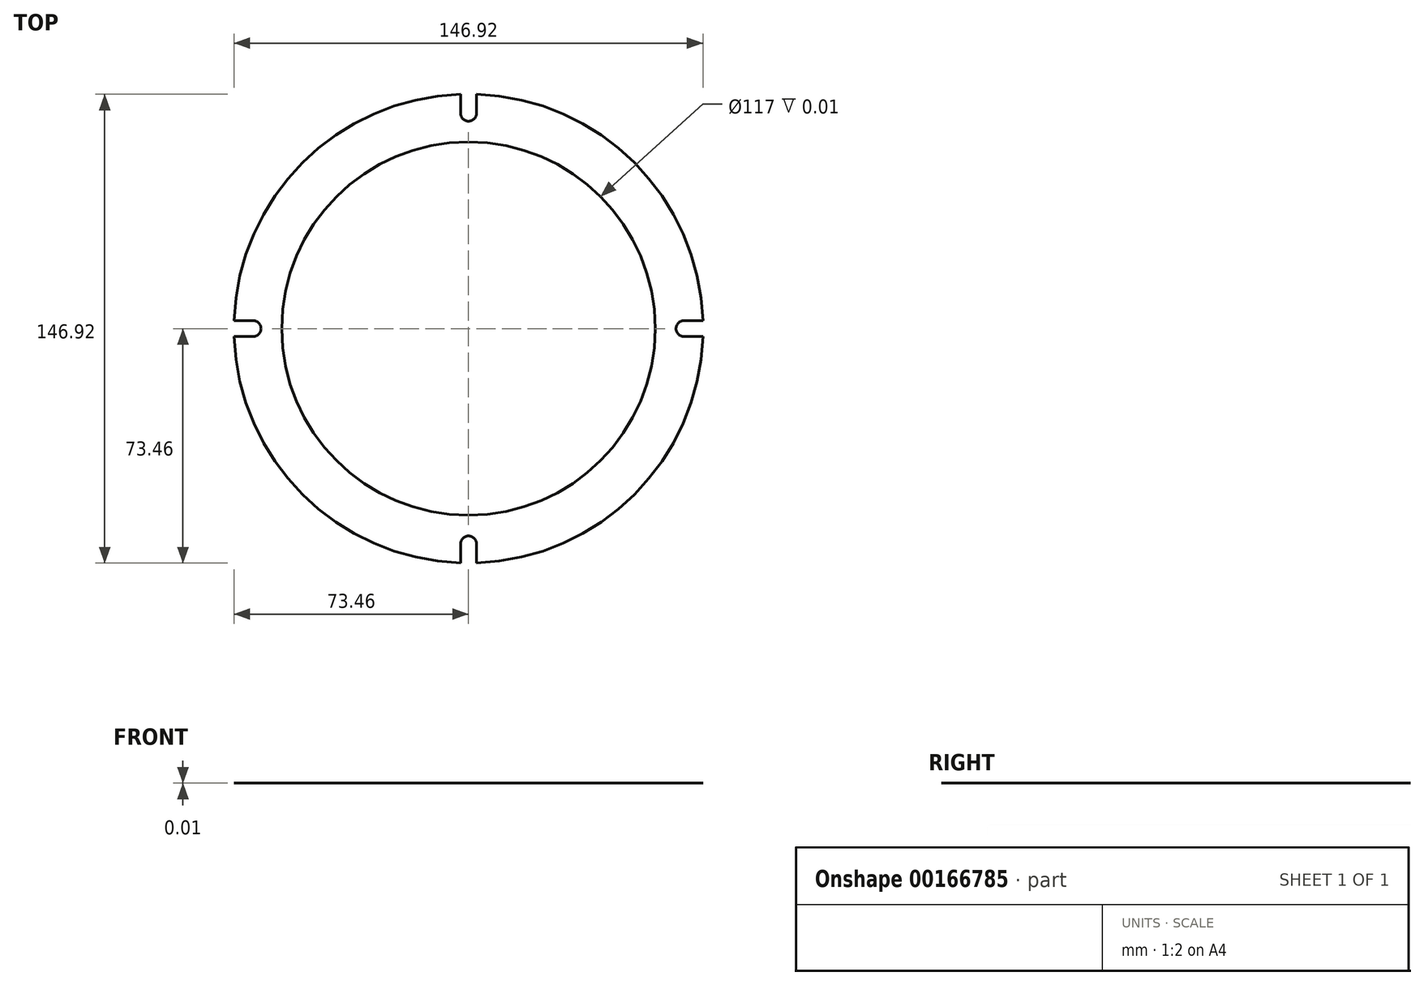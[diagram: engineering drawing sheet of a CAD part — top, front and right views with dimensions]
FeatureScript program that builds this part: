
annotation { "Feature Type Name" : "Feature", "Feature Type Description" : "" }
export const myFeature = defineFeature(function(context is Context, id is Id, definition is map)
    precondition{}
    {
        {
            var Q0;
            Q0=qCreatedBy(makeId("Top.planeOp"),FACE);
            var sketch = newSketch(context, id + "F0", { "sketchPlane" : qUnion([Q0])});
            skCircle(sketch, "E0", {"center": v(0, 0) * mm, "radius": 58.5 * mm});
            skCircle(sketch, "E1", {"center": v(0, 0) * mm, "radius": 73.5 * mm});
            skCircle(sketch, "E2", {"center": v(67.5, 0) * mm, "radius": 2.5 * mm});
            skCircle(sketch, "E3.1.0", {"center": v(0, 67.5) * mm, "radius": 2.5 * mm});
            skCircle(sketch, "E3.2.0", {"center": v(-67.5, 0) * mm, "radius": 2.5 * mm});
            skCircle(sketch, "E3.3.0", {"center": v(0, -67.5) * mm, "radius": 2.5 * mm});
            skLineSegment(sketch, "E4", {"start": v(67.5, -2.5) * mm, "end": v(73.46, -2.5) * mm});
            skLineSegment(sketch, "E5", {"start": v(67.5, 2.5) * mm, "end": v(73.46, 2.5) * mm});
            skLineSegment(sketch, "E6.1.0", {"start": v(-2.5, 67.5) * mm, "end": v(-2.5, 73.46) * mm});
            skLineSegment(sketch, "E6.1.1", {"start": v(2.5, 67.5) * mm, "end": v(2.5, 73.46) * mm});
            skLineSegment(sketch, "E6.2.0", {"start": v(-67.5, -2.5) * mm, "end": v(-73.46, -2.5) * mm});
            skLineSegment(sketch, "E6.2.1", {"start": v(-67.5, 2.5) * mm, "end": v(-73.46, 2.5) * mm});
            skLineSegment(sketch, "E6.3.0", {"start": v(2.5, -67.5) * mm, "end": v(2.5, -73.46) * mm});
            skLineSegment(sketch, "E6.3.1", {"start": v(-2.5, -67.5) * mm, "end": v(-2.5, -73.46) * mm});
            skSolve(sketch);
        }
        {
            var Q0;
            Q0=makeQuery(id+"F0.imprint","IMPRINT",FACE,{"disambiguationData":[TD([[makeQuery(id+"F0.imprint","IMPRINT",EDGE,{"derivedFrom":sQuery(id+"F0.wireOp",EDGE,"E0")}),-1.0]])]});
            extrude(context, id + "F1", {"entities" : qUnion([Q0]), "depth" : 1 / 101.6 * mm});
        }
    });
